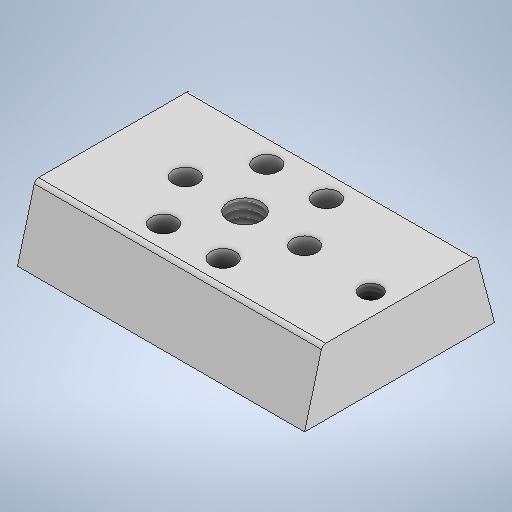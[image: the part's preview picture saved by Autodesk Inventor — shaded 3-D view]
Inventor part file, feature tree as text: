
AUTODESK INVENTOR PART (.ipt)
format: ipt  version: 2025 (Build 290162000, 162)  size: 286,720 bytes
history: native  units: mm
features: sketch x6, extrude x5, thread x2, chamfer x1, fillet x1
ambient origin geometry x8: Origin, YZ Plane, XZ Plane, XY Plane, X Axis, Y Axis, Z Axis, Center Point
bodies: Solid1 (feature_tree)
feature tree (15):
  extrude  "Extrusion1"  Depth=65.0mm
  extrude  "Extrusion2"  Depth=15.0mm
  extrude  "Extrusion3"  Depth=10.0mm
  thread  "Thread1"  [1 undecoded]
  extrude  "Extrusion4"  Depth=7.0mm TaperAngle=0.0deg
  thread  "Thread2"  [1 undecoded]
  chamfer  "Chamfer1"  Distance=8.0mm
  fillet  "Fillet1"  Radius=8.0mm
  extrude  "Extrusion5"  Depth=15.0mm
  sketch  "Sketch1"  dims[d0=65.0mm d1=43.0mm]
  sketch  "Sketch2"  dims[d5=6.5mm d6=10.0mm d7=5.0mm]
  sketch  "Sketch3"  dims[d8=5.0mm d9=7.0mm d10=0.0mm d11=7.5mm]
  sketch  "Sketch4"  dims[d12=25.0mm]
  sketch  "Sketch5"  dims[d13=15.0mm d14=8.0mm d15=0.0mm d16=8.0mm d17=0.0mm d18=4.7mm d19=20.0mm d20=5.0mm d21=15.0mm d22=0.0mm d23=15.0mm d24=0.0mm d25=4.0mm d26=15.0mm d27=12.217305mm d28=1.0mm d29=5.5mm d30=13.5mm d31=60.0mm d33=360.0deg d35=15.0mm d36=0.0mm]
  sketch  "Sketch Circular Pattern1"  dims[d2=15.0mm d3=0.0mm d4=6.5mm]
note: 2 required parameter values undecoded (feature->parameter linkage not recoverable at this tier; creation-order binding heuristic only, values carry confidence <= 0.55)
